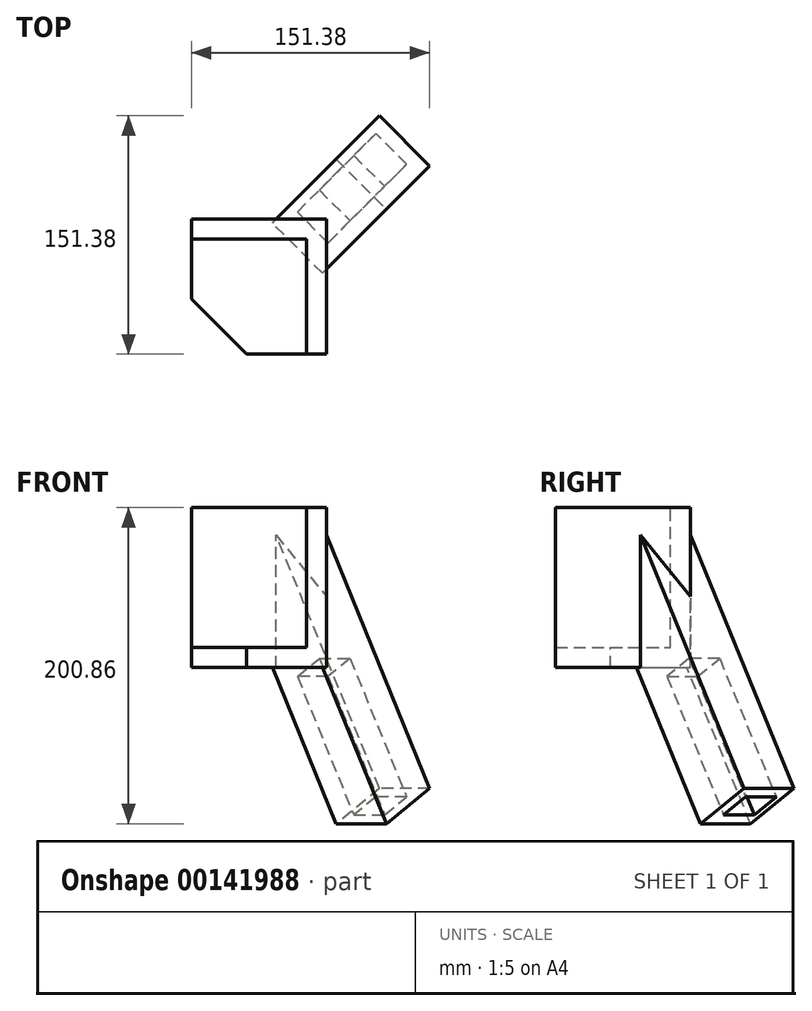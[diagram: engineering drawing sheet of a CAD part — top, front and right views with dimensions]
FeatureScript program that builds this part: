
annotation { "Feature Type Name" : "Feature", "Feature Type Description" : "" }
export const myFeature = defineFeature(function(context is Context, id is Id, definition is map)
    precondition{}
    {
        {
            var Q0;
            Q0=qCreatedBy(makeId("Top.planeOp"),FACE);
            var sketch = newSketch(context, id + "F0", { "sketchPlane" : qUnion([Q0])});
            skLineSegment(sketch, "E0.bottom", {"start": v(42.86, -42.86) * mm, "end": v(-42.86, -42.86) * mm});
            skLineSegment(sketch, "E0.top", {"start": v(42.86, 42.86) * mm, "end": v(-42.86, 42.86) * mm});
            skLineSegment(sketch, "E0.left", {"start": v(42.86, -42.86) * mm, "end": v(42.86, 42.86) * mm});
            skLineSegment(sketch, "E0.right", {"start": v(-42.86, -42.86) * mm, "end": v(-42.86, 42.86) * mm});
            skPoint(sketch, "E0.middle", {"position": v(0, 0) * mm});
            skSolve(sketch);
        }
        {
            var Q0;
            Q0 = qSketchRegion(id + "F0", true);
            extrude(context, id + "F1", {"entities" : qUnion([Q0]), "depth" : 101.6 * mm});
        }
        {
            var Q0;
            Q0=makeQuery(id+"F1.opExtrude","CAP_FACE",FACE,{"disambiguationData":[OSD([sQuery(id+"F0.wireOp",EDGE,"E0.bottom"),sQuery(id+"F0.wireOp",EDGE,"E0.top"),sQuery(id+"F0.wireOp",EDGE,"E0.left"),sQuery(id+"F0.wireOp",EDGE,"E0.right")])],"isStart":false});
            var sketch = newSketch(context, id + "F2", { "sketchPlane" : qUnion([Q0])});
            skLineSegment(sketch, "E1.0", {"start": v(30.16, -42.86) * mm, "end": v(30.16, 30.16) * mm});
            skLineSegment(sketch, "E2.0", {"start": v(30.16, 30.16) * mm, "end": v(-42.86, 30.16) * mm});
            skLineSegment(sketch, "E3", {"start": v(-42.86, 30.16) * mm, "end": v(-42.86, -42.86) * mm});
            skLineSegment(sketch, "E4", {"start": v(-42.86, -42.86) * mm, "end": v(30.16, -42.86) * mm});
            skSolve(sketch);
        }
        {
            var Q0;
            Q0 = qSketchRegion(id + "F2", true);
            extrude(context, id + "F3", {"entities" : qUnion([Q0]), "operationType" : NewBodyOperationType.REMOVE, "oppositeDirection" : true, "depth" : 88.9 * mm});
        }
        {
            var Q0;
            Q0=makeQuery(id+"F3.boolean.opBoolean","COPY",FACE,{"derivedFrom":makeQuery(id+"F3.opExtrude","CAP_FACE",FACE,{"disambiguationData":[OSD([sQuery(id+"F2.wireOp",EDGE,"E1.0"),sQuery(id+"F2.wireOp",EDGE,"E2.0"),sQuery(id+"F2.wireOp",EDGE,"E3"),sQuery(id+"F2.wireOp",EDGE,"E4")])],"isStart":false})});
            var sketch = newSketch(context, id + "F4", { "sketchPlane" : qUnion([Q0])});
            skLineSegment(sketch, "E5", {"start": v(-7.94, -42.86) * mm, "end": v(-42.86, -7.94) * mm});
            skLineSegment(sketch, "E6.0", {"start": v(-42.86, -42.86) * mm, "end": v(-42.86, -7.94) * mm});
            skPoint(sketch, "E7.orphan", {"position": v(-42.86, 30.16) * mm});
            skPoint(sketch, "E8.0.start.orphan", {"position": v(42.86, -42.86) * mm});
            skLineSegment(sketch, "E9", {"start": v(-42.86, -42.86) * mm, "end": v(-7.94, -42.86) * mm});
            skSolve(sketch);
        }
        {
            var Q0;
            Q0 = qSketchRegion(id + "F4", true);
            extrude(context, id + "F5", {"entities" : qUnion([Q0]), "operationType" : NewBodyOperationType.REMOVE, "oppositeDirection" : true, "depth" : 25.4 * mm});
        }
        {
            var Q0;
            Q0=makeQuery(id+"F3.boolean.opBoolean","COPY",VERTEX,{"derivedFrom":makeQuery(id+"F3.opExtrude","CAP_VERTEX",VERTEX,{"disambiguationData":[OSD([sQuery(id+"F2.wireOp",EDGE,"E1.0"),sQuery(id+"F2.wireOp",EDGE,"E2.0")])],"isStart":true})});
            var Q1;
            Q1=makeQuery(id+"F1.opExtrude","CAP_VERTEX",VERTEX,{"disambiguationData":[OSD([sQuery(id+"F0.wireOp",EDGE,"E0.top"),sQuery(id+"F0.wireOp",EDGE,"E0.left")])],"isStart":false});
            var Q2;
            Q2=makeQuery(id+"F1.opExtrude","CAP_VERTEX",VERTEX,{"disambiguationData":[OSD([sQuery(id+"F0.wireOp",EDGE,"E0.top"),sQuery(id+"F0.wireOp",EDGE,"E0.left")])],"isStart":true});
            cPlane(context, id + "F6", {"entities" : qUnion([Q0, Q1, Q2]), "cplaneType" : CPlaneType.THREE_POINT, "offset" : 25.4 * mm, "width" : 152.4 * mm, "height" : 152.4 * mm});
        }
        {
            var Q0;
            Q0=qCreatedBy(id+"F6.planeOp",FACE);
            var sketch = newSketch(context, id + "F7", { "sketchPlane" : qUnion([Q0])});
            skLineSegment(sketch, "E10.0", {"start": v(60.62, 101.6) * mm, "end": v(60.62, 0) * mm});
            skLineSegment(sketch, "E10.1", {"start": v(0, 0) * mm, "end": v(60.62, 0) * mm});
            skLineSegment(sketch, "E11", {"start": v(60.62, 0) * mm, "end": v(97.25, -63.45) * mm});
            skSolve(sketch);
        }
        {
            var Q0;
            Q0=qCreatedBy(makeId("Top.planeOp"),FACE);
            var sketch = newSketch(context, id + "F8", { "sketchPlane" : qUnion([Q0])});
            skLineSegment(sketch, "E12.0.0", {"start": v(42.86, -42.86) * mm, "end": v(-7.94, -42.86) * mm});
            skLineSegment(sketch, "E12.0.1", {"start": v(-7.94, -42.86) * mm, "end": v(-42.86, -7.94) * mm});
            skLineSegment(sketch, "E12.0.2", {"start": v(-42.86, -7.94) * mm, "end": v(-42.86, 42.86) * mm});
            skLineSegment(sketch, "E12.0.3", {"start": v(-42.86, 42.86) * mm, "end": v(42.86, 42.86) * mm});
            skLineSegment(sketch, "E12.0.4", {"start": v(42.86, 42.86) * mm, "end": v(42.86, -42.86) * mm});
            skPoint(sketch, "E13.orphan", {"position": v(42.86, 42.86) * mm});
            skSolve(sketch);
        }
        {
            var Q0;
            Q0=sQuery(id+"F8.wireOp",VERTEX,"E13.orphan");
            var Q1;
            Q1=sQuery(id+"F7.wireOp",EDGE,"E11");
            cPlane(context, id + "F9", {"entities" : qUnion([Q0, Q1]), "cplaneType" : CPlaneType.LINE_POINT, "offset" : 25.4 * mm, "width" : 152.4 * mm, "height" : 152.4 * mm});
        }
        {
            var Q0;
            Q0=qCreatedBy(id+"F9.planeOp",FACE);
            var sketch = newSketch(context, id + "F10", { "sketchPlane" : qUnion([Q0])});
            skLineSegment(sketch, "E14.0", {"start": v(32.08, -71.47) * mm, "end": v(2.58, -37.4) * mm});
            skLineSegment(sketch, "E14.1", {"start": v(2.58, -37.4) * mm, "end": v(36.65, -7.9) * mm});
            skLineSegment(sketch, "E14.2", {"start": v(36.65, -7.9) * mm, "end": v(66.16, -41.97) * mm});
            skLineSegment(sketch, "E14.3", {"start": v(66.16, -41.97) * mm, "end": v(32.08, -71.47) * mm});
            skPoint(sketch, "E14.0.midPoint", {"position": v(17.33, -54.44) * mm});
            skLineSegment(sketch, "E15.0", {"start": v(14.65, -41.64) * mm, "end": v(35.52, -23.57) * mm});
            skLineSegment(sketch, "E16.0", {"start": v(29.6, -58.91) * mm, "end": v(14.65, -41.64) * mm});
            skLineSegment(sketch, "E17.trimOffspring", {"start": v(50.48, -40.84) * mm, "end": v(29.6, -58.91) * mm});
            skLineSegment(sketch, "E18.trimOffspring", {"start": v(35.52, -23.57) * mm, "end": v(50.48, -40.84) * mm});
            skPoint(sketch, "E19.orphan", {"position": v(67.62, -78.08) * mm});
            skPoint(sketch, "E20.orphan", {"position": v(34.37, -39.68) * mm});
            skSolve(sketch);
        }
        {
            var Q0;
            Q0=makeQuery(id+"F10.imprint","IMPRINT",FACE,{"disambiguationData":[TD([[makeQuery(id+"F10.imprint","IMPRINT",EDGE,{"derivedFrom":sQuery(id+"F10.wireOp",EDGE,"E15.0")}),-1.0]])]});
            var Q1;
            Q1=makeQuery(id+"F10.imprint","IMPRINT",FACE,{"disambiguationData":[TD([[makeQuery(id+"F10.imprint","IMPRINT",EDGE,{"derivedFrom":sQuery(id+"F10.wireOp",EDGE,"E14.0")}),-1.0]])]});
            extrude(context, id + "F11", {"entities" : qUnion([Q0, Q1]), "operationType" : NewBodyOperationType.ADD, "depth" : 101.6 * mm, "hasSecondDirection" : true, "secondDirectionBound" : SecondDirectionBoundingType.UP_TO_NEXT, "secondDirectionOppositeDirection" : true, "secondDirectionDepth" : 25.4 * mm});
        }
        {
            var Q0;
            Q0 = qSketchRegion(id + "F10", true);
            extrude(context, id + "F12", {"entities" : qUnion([Q0]), "operationType" : NewBodyOperationType.ADD, "depth" : 101.6 * mm});
        }
        {
            var Q0;
            Q0=makeQuery(id+"F11.opExtrude","CAP_FACE",FACE,{"disambiguationData":[OSD([sQuery(id+"F10.wireOp",EDGE,"E14.0"),sQuery(id+"F10.wireOp",EDGE,"E14.1"),sQuery(id+"F10.wireOp",EDGE,"E14.2"),sQuery(id+"F10.wireOp",EDGE,"E14.3")])],"isStart":false});
            var sketch = newSketch(context, id + "F13", { "sketchPlane" : qUnion([Q0])});
            skLineSegment(sketch, "E21.0", {"start": v(50.48, -40.84) * mm, "end": v(29.6, -58.91) * mm});
            skLineSegment(sketch, "E22.0", {"start": v(35.52, -23.57) * mm, "end": v(50.48, -40.84) * mm});
            skLineSegment(sketch, "E23.0", {"start": v(14.65, -41.64) * mm, "end": v(35.52, -23.57) * mm});
            skLineSegment(sketch, "E24.0", {"start": v(29.6, -58.91) * mm, "end": v(14.65, -41.64) * mm});
            skSolve(sketch);
        }
        {
            var Q0;
            Q0=makeQuery(id+"F13.imprint","IMPRINT",FACE,{"disambiguationData":[TD([[makeQuery(id+"F13.imprint","IMPRINT",EDGE,{"derivedFrom":sQuery(id+"F13.wireOp",EDGE,"E21.0")}),-1.0]])]});
            var Q1;
            Q1=qCreatedBy(id+"F9.planeOp",FACE);
            extrude(context, id + "F14", {"entities" : qUnion([Q0]), "operationType" : NewBodyOperationType.REMOVE, "endBound" : BoundingType.UP_TO_SURFACE, "oppositeDirection" : true, "endBoundEntityFace" : qUnion([Q1]), "depth" : 25.4 * mm});
        }
    });
